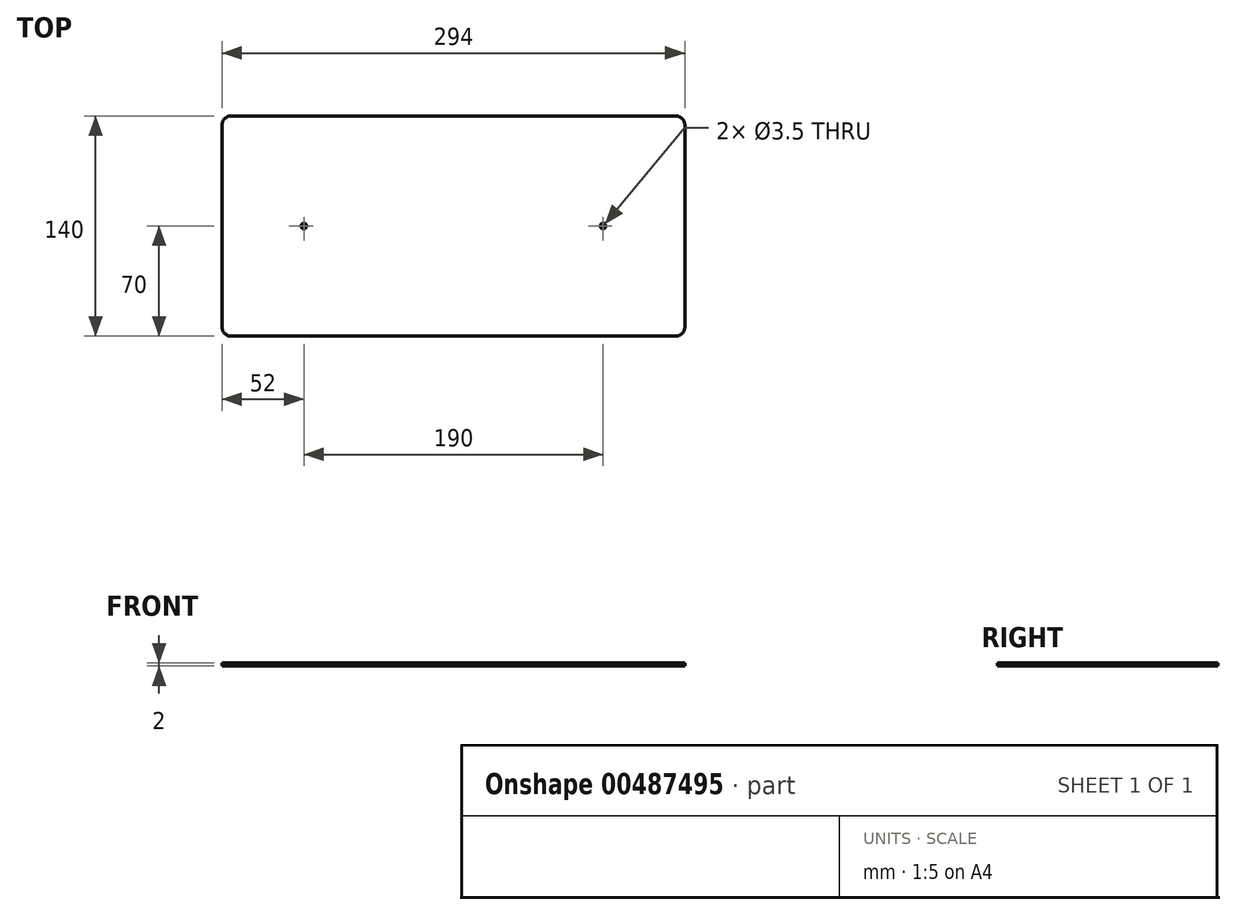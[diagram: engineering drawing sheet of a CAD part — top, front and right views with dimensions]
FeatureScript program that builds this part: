
annotation { "Feature Type Name" : "Feature", "Feature Type Description" : "" }
export const myFeature = defineFeature(function(context is Context, id is Id, definition is map)
    precondition{}
    {
        {
            var Q0;
            Q0=qCreatedBy(makeId("Top.planeOp"),FACE);
            var sketch = newSketch(context, id + "F0", { "sketchPlane" : qUnion([Q0])});
            skLineSegment(sketch, "E0.bottom", {"start": v(147, 70) * mm, "end": v(-147, 70) * mm});
            skLineSegment(sketch, "E0.top", {"start": v(147, -70) * mm, "end": v(-147, -70) * mm});
            skLineSegment(sketch, "E0.left", {"start": v(147, 70) * mm, "end": v(147, -70) * mm});
            skLineSegment(sketch, "E0.right", {"start": v(-147, 70) * mm, "end": v(-147, -70) * mm});
            skPoint(sketch, "E0.middle", {"position": v(0, 0) * mm});
            skSolve(sketch);
        }
        {
            var Q0;
            Q0=makeQuery(id+"F0.imprint","IMPRINT",FACE,{"disambiguationData":[TD([[makeQuery(id+"F0.imprint","IMPRINT",EDGE,{"derivedFrom":sQuery(id+"F0.wireOp",EDGE,"E0.bottom")}),1.0]])]});
            extrude(context, id + "F1", {"entities" : qUnion([Q0]), "depth" : 2 * mm});
        }
        {
            var Q0;
            Q0=makeQuery(id+"F1.opExtrude","SWEPT_EDGE",EDGE,{"disambiguationData":[OSD([sQuery(id+"F0.wireOp",EDGE,"E0.top"),sQuery(id+"F0.wireOp",EDGE,"E0.left")])]});
            var Q1;
            Q1=makeQuery(id+"F1.opExtrude","SWEPT_EDGE",EDGE,{"disambiguationData":[OSD([sQuery(id+"F0.wireOp",EDGE,"E0.bottom"),sQuery(id+"F0.wireOp",EDGE,"E0.left")])]});
            var Q2;
            Q2=makeQuery(id+"F1.opExtrude","SWEPT_EDGE",EDGE,{"disambiguationData":[OSD([sQuery(id+"F0.wireOp",EDGE,"E0.top"),sQuery(id+"F0.wireOp",EDGE,"E0.right")])]});
            var Q3;
            Q3=makeQuery(id+"F1.opExtrude","SWEPT_EDGE",EDGE,{"disambiguationData":[OSD([sQuery(id+"F0.wireOp",EDGE,"E0.bottom"),sQuery(id+"F0.wireOp",EDGE,"E0.right")])]});
            fillet(context, id + "F2", {"entities" : qUnion([Q0, Q1, Q2, Q3]), "radius" : 6 * mm, "tangentPropagation" : true, "allowEdgeOverflow" : false});
        }
        {
            var Q0;
            Q0=makeQuery(id+"F1.opExtrude","CAP_FACE",FACE,{"disambiguationData":[OSD([sQuery(id+"F0.wireOp",EDGE,"E0.bottom"),sQuery(id+"F0.wireOp",EDGE,"E0.top"),sQuery(id+"F0.wireOp",EDGE,"E0.left"),sQuery(id+"F0.wireOp",EDGE,"E0.right")])],"isStart":true});
            var sketch = newSketch(context, id + "F3", { "sketchPlane" : qUnion([Q0])});
            skLineSegment(sketch, "E1", {"start": v(-95, 0) * mm, "end": v(95, 0) * mm, "construction": true});
            skPoint(sketch, "E2", {"position": v(0, 0) * mm});
            skCircle(sketch, "E3", {"center": v(-95, 0) * mm, "radius": 1.75 * mm});
            skCircle(sketch, "E4", {"center": v(95, 0) * mm, "radius": 1.75 * mm});
            skSolve(sketch);
        }
        {
            var Q0;
            Q0 = qSketchRegion(id + "F3", true);
            extrude(context, id + "F4", {"entities" : qUnion([Q0]), "operationType" : NewBodyOperationType.REMOVE, "endBound" : BoundingType.UP_TO_NEXT, "oppositeDirection" : true, "depth" : 25 * mm});
        }
    });
